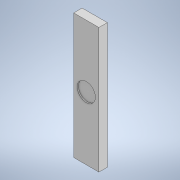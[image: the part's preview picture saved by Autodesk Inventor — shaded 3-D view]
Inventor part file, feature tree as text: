
AUTODESK INVENTOR PART (.ipt)
format: ipt  version: 2021.2 (Build 252289000, 289)  size: 112,640 bytes
history: native  units: in
note: dims shown in document units (in); Inventor stores cm internally (conversion verified against a paired STEP export)
features: extrude x3, sketch x3, other x3, plane x1
ambient origin geometry x8: Origin, YZ Plane, XZ Plane, XY Plane, X Axis, Y Axis, Z Axis, Center Point
bodies: Solid1 (feature_tree)
feature tree (10):
  plane  "Work Plane1"
  extrude  "Extrusion1"  Depth=6.0in
  extrude  "Extrusion2"  Depth=0.4in
  extrude  "Extrusion3"  Depth=0.0625in TaperAngle=0.0deg
  sketch  "Sketch1"  dims[d0=1.2in d1=6.0in]
  sketch  "Sketch2"  dims[d2=0.4in d3=0.0in d4=0.87in]
  sketch  "Sketch3"  dims[d5=0.0625in d6=0.0in d7=0.04in d8=0.0in]
  other  "<userpath>\OneDrive\Desktop\general python\turret\cameraarm\v2\assembly.iam"
  other  "assembly.iam"
  other  "servoarm:1"
